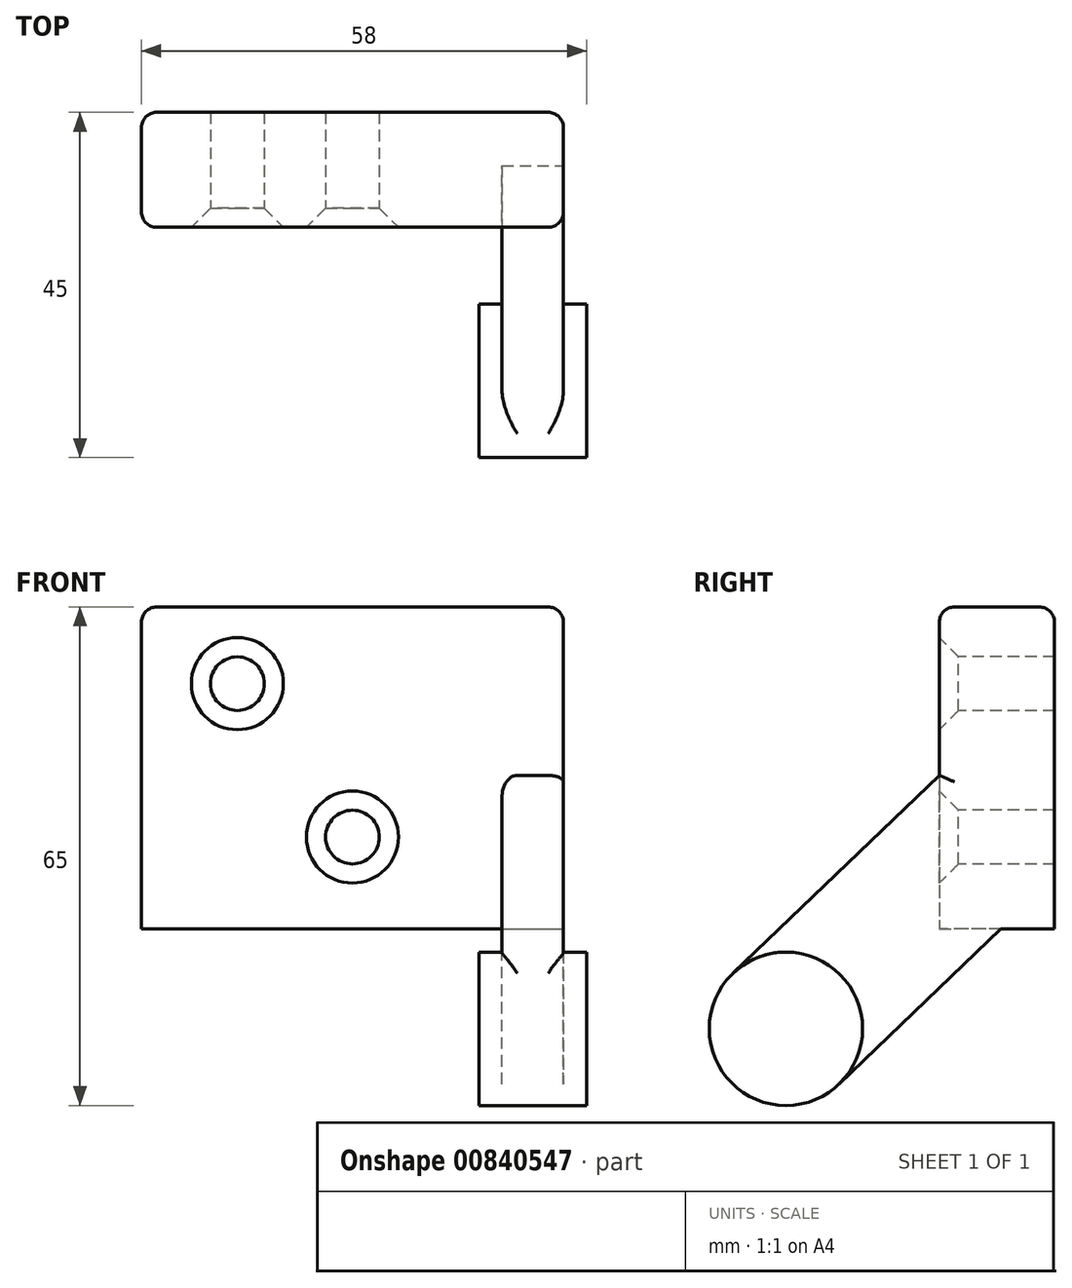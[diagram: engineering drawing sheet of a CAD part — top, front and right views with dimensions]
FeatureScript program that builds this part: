
annotation { "Feature Type Name" : "Feature", "Feature Type Description" : "" }
export const myFeature = defineFeature(function(context is Context, id is Id, definition is map)
    precondition{}
    {
        {
            var Q0;
            Q0=qCreatedBy(makeId("Front.planeOp"),FACE);
            var sketch = newSketch(context, id + "F0", { "sketchPlane" : qUnion([Q0])});
            skLineSegment(sketch, "E0.bottom", {"start": v(-27.5, 0) * mm, "end": v(27.5, 0) * mm});
            skLineSegment(sketch, "E0.top", {"start": v(-27.5, -42) * mm, "end": v(27.5, -42) * mm});
            skLineSegment(sketch, "E0.left", {"start": v(-27.5, 0) * mm, "end": v(-27.5, -42) * mm});
            skLineSegment(sketch, "E0.right", {"start": v(27.5, 0) * mm, "end": v(27.5, -42) * mm});
            skSolve(sketch);
        }
        {
            var Q0;
            Q0=makeQuery(id+"F0.imprint","IMPRINT",FACE,{"disambiguationData":[TD([[makeQuery(id+"F0.imprint","IMPRINT",EDGE,{"derivedFrom":sQuery(id+"F0.wireOp",EDGE,"E0.bottom")}),-1.0]])]});
            extrude(context, id + "F1", {"entities" : qUnion([Q0]), "oppositeDirection" : true, "depth" : 15 * mm, "offsetDistance" : 25 * mm});
        }
        {
            var Q0;
            Q0=makeQuery(id+"F1.opExtrude","SWEPT_FACE",FACE,{"disambiguationData":[OSD([sQuery(id+"F0.wireOp",EDGE,"E0.right")])]});
            var sketch = newSketch(context, id + "F2", { "sketchPlane" : qUnion([Q0])});
            skLineSegment(sketch, "E1", {"start": v(0, -21.96) * mm, "end": v(-26.92, -47.78) * mm});
            skLineSegment(sketch, "E2", {"start": v(-26.92, -47.78) * mm, "end": v(-13.08, -62.22) * mm});
            skLineSegment(sketch, "E3", {"start": v(-13.08, -62.22) * mm, "end": v(8, -42) * mm});
            skCircle(sketch, "E4", {"center": v(-20, -55) * mm, "radius": 10 * mm});
            skSolve(sketch);
        }
        {
            var Q0;
            {var subQ7=sQuery(id+"F2.wireOp",EDGE,"E1");Q0=makeQuery(id+"F2.imprint","IMPRINT",FACE,{"disambiguationData":[TD([[makeQuery(id+"F2.imprint","IMPRINT",EDGE,{"derivedFrom":subQ7}),1.0]])]});}
            var Q1;
            {var subQ0=sQuery(id+"F2.wireOp",EDGE,"E2");Q1=makeQuery(id+"F2.imprint","IMPRINT",FACE,{"disambiguationData":[TD([[makeQuery(id+"F2.imprint","IMPRINT",EDGE,{"derivedFrom":subQ0}),1.0]])]});}
            extrude(context, id + "F3", {"entities" : qUnion([Q0, Q1]), "operationType" : NewBodyOperationType.ADD, "oppositeDirection" : true, "depth" : 8 * mm, "offsetDistance" : 25 * mm});
        }
        {
            var Q0;
            {var subQ0=sQuery(id+"F2.wireOp",EDGE,"E2");Q0=makeQuery(id+"F2.imprint","IMPRINT",FACE,{"disambiguationData":[TD([[makeQuery(id+"F2.imprint","IMPRINT",EDGE,{"derivedFrom":subQ0}),-1.0]])]});}
            var Q1;
            {var subQ0=sQuery(id+"F2.wireOp",EDGE,"E2");Q1=makeQuery(id+"F2.imprint","IMPRINT",FACE,{"disambiguationData":[TD([[makeQuery(id+"F2.imprint","IMPRINT",EDGE,{"derivedFrom":subQ0}),1.0]])]});}
            extrude(context, id + "F4", {"entities" : qUnion([Q0, Q1]), "operationType" : NewBodyOperationType.ADD, "depth" : 3 * mm, "offsetDistance" : 25 * mm, "hasSecondDirection" : true, "secondDirectionOppositeDirection" : true, "secondDirectionDepth" : 11 * mm});
        }
        {
            var Q0;
            Q0=makeQuery(id+"F1.opExtrude","CAP_FACE",FACE,{"disambiguationData":[OSD([sQuery(id+"F0.wireOp",EDGE,"E0.bottom"),sQuery(id+"F0.wireOp",EDGE,"E0.top"),sQuery(id+"F0.wireOp",EDGE,"E0.left"),sQuery(id+"F0.wireOp",EDGE,"E0.right")])],"isStart":true});
            var sketch = newSketch(context, id + "F5", { "sketchPlane" : qUnion([Q0])});
            skPoint(sketch, "E5", {"position": v(-15, -10) * mm});
            skPoint(sketch, "E6", {"position": v(0, -30) * mm});
            skSolve(sketch);
        }
        {
            var Q0;
            Q0=sQuery(id+"F5.wireOp",VERTEX,"E5");
            var Q1;
            Q1=sQuery(id+"F5.wireOp",VERTEX,"E6");
            var Q2;
            Q2=makeQuery(id+"F1.opExtrude","SWEPT_BODY",BODY,{"disambiguationData":[OSD([sQuery(id+"F0.wireOp",EDGE,"E0.bottom"),sQuery(id+"F0.wireOp",EDGE,"E0.top"),sQuery(id+"F0.wireOp",EDGE,"E0.left"),sQuery(id+"F0.wireOp",EDGE,"E0.right")])]});
            hole(context, id + "F6", {"style" : HoleStyle.C_SINK, "endStyle" : HoleEndStyle.THROUGH, "holeDiameter" : 7 * mm, "cSinkDiameter" : 12 * mm, "cSinkAngle" : 90 * degree, "majorDiameter" : 5 * mm, "isTappedThrough" : true, "tappedDepth" : 12 * mm, "tapClearance" : 3, "locations" : qUnion([Q0, Q1]), "scope" : qUnion([Q2])});
        }
        {
            var Q0;
            Q0=makeQuery(id+"F1.opExtrude","CAP_EDGE",EDGE,{"disambiguationData":[OSD([sQuery(id+"F0.wireOp",EDGE,"E0.bottom")])],"isStart":false});
            var Q1;
            Q1=makeQuery(id+"F1.opExtrude","CAP_EDGE",EDGE,{"disambiguationData":[OSD([sQuery(id+"F0.wireOp",EDGE,"E0.bottom")])],"isStart":true});
            var Q2;
            Q2=makeQuery(id+"Fr7BSbmkyWbJ9hy_1.1.F3.opExtrude","SWEPT_EDGE",EDGE,{"disambiguationData":[OSD([sQuery(id+"F0.wireOp",EDGE,"E0.right"),sQuery(id+"F2.wireOp",EDGE,"E1")])]});
            var Q3;
            Q3=makeQuery(id+"F3.opExtrude","SWEPT_EDGE",EDGE,{"disambiguationData":[OSD([sQuery(id+"F0.wireOp",EDGE,"E0.right"),sQuery(id+"F2.wireOp",EDGE,"E1")])]});
            fillet(context, id + "F7", {"entities" : qUnion([Q0, Q1, Q2, Q3]), "radius" : 2 * mm, "tangentPropagation" : true, "allowEdgeOverflow" : false});
        }
        {
            var Q0;
            Q0=makeQuery(id+"F1.opExtrude","SWEPT_EDGE",EDGE,{"disambiguationData":[OSD([sQuery(id+"F0.wireOp",EDGE,"E0.bottom"),sQuery(id+"F0.wireOp",EDGE,"E0.left")])]});
            var Q1;
            Q1=makeQuery(id+"F1.opExtrude","SWEPT_EDGE",EDGE,{"disambiguationData":[OSD([sQuery(id+"F0.wireOp",EDGE,"E0.bottom"),sQuery(id+"F0.wireOp",EDGE,"E0.right")])]});
            var Q2;
            Q2=makeQuery(id+"Fr7BSbmkyWbJ9hy_1.1.F3.opExtrude","CAP_EDGE",EDGE,{"disambiguationData":[OSD([sQuery(id+"F2.wireOp",EDGE,"E1")])],"isStart":false});
            var Q3;
            Q3=makeQuery(id+"Fr7BSbmkyWbJ9hy_1.1.F3.opExtrude","CAP_EDGE",EDGE,{"disambiguationData":[OSD([sQuery(id+"F2.wireOp",EDGE,"E1")])],"isStart":true});
            var Q4;
            Q4=makeQuery(id+"F3.opExtrude","CAP_EDGE",EDGE,{"disambiguationData":[OSD([sQuery(id+"F2.wireOp",EDGE,"E1")])],"isStart":false});
            var Q5;
            Q5=makeQuery(id+"F3.opExtrude","CAP_EDGE",EDGE,{"disambiguationData":[OSD([sQuery(id+"F2.wireOp",EDGE,"E1")])],"isStart":true});
            fillet(context, id + "F8", {"entities" : qUnion([Q0, Q1, Q2, Q3, Q4, Q5]), "radius" : 2 * mm, "tangentPropagation" : true, "allowEdgeOverflow" : false});
        }
    });
